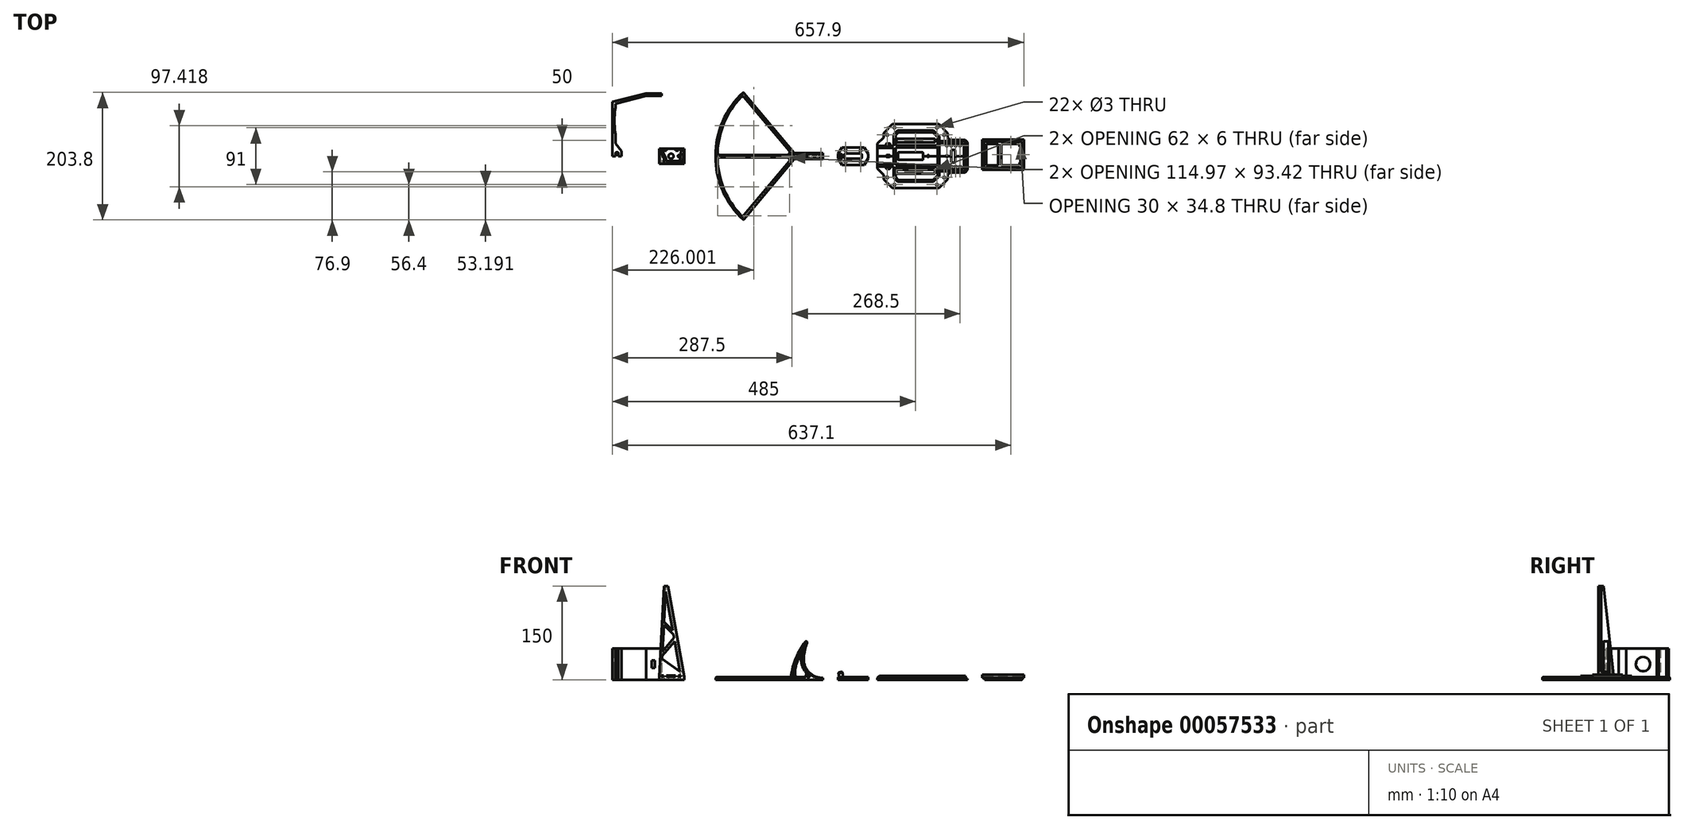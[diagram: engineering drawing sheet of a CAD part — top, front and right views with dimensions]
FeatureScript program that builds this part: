
annotation { "Feature Type Name" : "Feature", "Feature Type Description" : "" }
export const myFeature = defineFeature(function(context is Context, id is Id, definition is map)
    precondition{}
    {
        {
            var Q0;
            Q0=qCreatedBy(makeId("Front.planeOp"),FACE);
            var sketch = newSketch(context, id + "F0", { "sketchPlane" : qUnion([Q0])});
            skArc(sketch, "E0", {"start": v(23.8, 60.9) * mm, "mid": v(7.67, 32.1) * mm, "end": v(0, 0) * mm});
            skLineSegment(sketch, "E1", {"start": v(0, 0) * mm, "end": v(52, 0) * mm});
            skLineSegment(sketch, "E2", {"start": v(52, 0) * mm, "end": v(52, 3) * mm});
            skLineSegment(sketch, "E3", {"start": v(52, 3) * mm, "end": v(51, 3) * mm});
            skCircle(sketch, "E4", {"center": v(28.5, 4.8) * mm, "radius": 1.5 * mm});
            skArc(sketch, "E5", {"start": v(11.94, 32) * mm, "mid": v(11.4, 30.63) * mm, "end": v(10.87, 29.26) * mm});
            skLineSegment(sketch, "E6", {"start": v(7, 4) * mm, "end": v(22.45, 4) * mm});
            skArc(sketch, "E7", {"start": v(17.05, 31.14) * mm, "mid": v(19.78, 19.53) * mm, "end": v(26.35, 9.58) * mm});
            skArc(sketch, "E8", {"start": v(17.05, 31.14) * mm, "mid": v(14.83, 33.62) * mm, "end": v(11.94, 32) * mm});
            skLineSegment(sketch, "E9", {"start": v(22.45, 4) * mm, "end": v(26.35, 9.58) * mm});
            skArc(sketch, "E10", {"start": v(21.24, 36.77) * mm, "mid": v(28.5, 13.16) * mm, "end": v(51, 3) * mm});
            skArc(sketch, "E11", {"start": v(21, 51.66) * mm, "mid": v(16.42, 43.88) * mm, "end": v(12.45, 35.77) * mm});
            skArc(sketch, "E12", {"start": v(17.98, 34.71) * mm, "mid": v(15.37, 36.06) * mm, "end": v(12.45, 35.77) * mm});
            skArc(sketch, "E13", {"start": v(26.43, 59.54) * mm, "mid": v(25.7, 61.33) * mm, "end": v(23.8, 60.9) * mm});
            skArc(sketch, "E14", {"start": v(21, 51.66) * mm, "mid": v(19.19, 43.24) * mm, "end": v(17.98, 34.71) * mm});
            skLineSegment(sketch, "E15", {"start": v(26.43, 59.54) * mm, "end": v(26.12, 58.59) * mm});
            skArc(sketch, "E16", {"start": v(26.12, 58.59) * mm, "mid": v(23.16, 47.8) * mm, "end": v(21.24, 36.77) * mm});
            skArc(sketch, "E17", {"start": v(10.87, 29.26) * mm, "mid": v(7.97, 18.8) * mm, "end": v(7, 8) * mm});
            skLineSegment(sketch, "E18", {"start": v(7, 4) * mm, "end": v(7, 8) * mm});
            skSolve(sketch);
        }
        {
            var Q0;
            Q0=makeQuery(id+"F0.imprint","IMPRINT",FACE,{"disambiguationData":[TD([[makeQuery(id+"F0.imprint","IMPRINT",EDGE,{"derivedFrom":sQuery(id+"F0.wireOp",EDGE,"E0")}),1.0]])]});
            extrude(context, id + "F1", {"entities" : qUnion([Q0]), "depth" : (9.5 / 2) * mm});
        }
        {
            var Q0;
            Q0=makeQuery(id+"F1.opExtrude","SWEPT_EDGE",EDGE,{"disambiguationData":[OSD([sQuery(id+"F0.wireOp",EDGE,"E11"),sQuery(id+"F0.wireOp",EDGE,"E14")])]});
            fillet(context, id + "F2", {"entities" : qUnion([Q0]), "radius" : 0.75 * mm, "tangentPropagation" : true, "allowEdgeOverflow" : false});
        }
        {
            var Q0;
            Q0=makeQuery(id+"F1.opExtrude","SWEPT_EDGE",EDGE,{"disambiguationData":[OSD([sQuery(id+"F0.wireOp",EDGE,"E7"),sQuery(id+"F0.wireOp",EDGE,"E9")])]});
            var Q1;
            Q1=makeQuery(id+"F1.opExtrude","SWEPT_EDGE",EDGE,{"disambiguationData":[OSD([sQuery(id+"F0.wireOp",EDGE,"E6"),sQuery(id+"F0.wireOp",EDGE,"E9")])]});
            fillet(context, id + "F3", {"entities" : qUnion([Q0, Q1]), "radius" : 4 * mm, "tangentPropagation" : true, "allowEdgeOverflow" : false});
        }
        {
            var Q0;
            Q0=makeQuery(id+"F1.opExtrude","SWEPT_EDGE",EDGE,{"disambiguationData":[OSD([sQuery(id+"F0.wireOp",EDGE,"E5"),sQuery(id+"F0.wireOp",EDGE,"E6")])]});
            fillet(context, id + "F4", {"entities" : qUnion([Q0]), "radius" : 5 * mm, "tangentPropagation" : true, "allowEdgeOverflow" : false});
        }
        {
            var Q0;
            Q0=makeQuery(id+"F1.opExtrude","CAP_EDGE",EDGE,{"disambiguationData":[OSD([sQuery(id+"F0.wireOp",EDGE,"E0")])],"isStart":false});
            var Q1;
            Q1=makeQuery(id+"F1.opExtrude","CAP_EDGE",EDGE,{"disambiguationData":[OSD([sQuery(id+"F0.wireOp",EDGE,"E5")])],"isStart":false});
            chamfer(context, id + "F5", {"entities" : qUnion([Q0, Q1]), "width" : 1 * mm, "tangentPropagation" : true});
        }
        {
            var Q0;
            Q0=qCreatedBy(makeId("Top.planeOp"),FACE);
            cPlane(context, id + "F6", {"entities" : qUnion([Q0]), "cplaneType" : CPlaneType.OFFSET, "offset" : 2 * mm, "width" : 150 * mm, "height" : 150 * mm});
        }
        {
            var Q0;
            Q0=qCreatedBy(makeId("Top.planeOp"),FACE);
            var sketch = newSketch(context, id + "F7", { "sketchPlane" : qUnion([Q0])});
            skCircle(sketch, "E19", {"center": v(2.5, 0) * mm, "radius": 1.5 * mm});
            skCircle(sketch, "E20", {"center": v(20.5, 0) * mm, "radius": 2.5 * mm});
            skCircle(sketch, "E21", {"center": v(38.5, 0) * mm, "radius": 2 * mm});
            skCircle(sketch, "E22", {"center": v(48.5, 0) * mm, "radius": 1.5 * mm});
            skSolve(sketch);
        }
        {
            var Q0;
            Q0=makeQuery(id+"F7.imprint","IMPRINT",FACE,{"disambiguationData":[TD([[makeQuery(id+"F7.imprint","IMPRINT",EDGE,{"derivedFrom":sQuery(id+"F7.wireOp",EDGE,"E20")}),1.0]])]});
            var Q1;
            Q1=makeQuery(id+"F7.imprint","IMPRINT",FACE,{"disambiguationData":[TD([[makeQuery(id+"F7.imprint","IMPRINT",EDGE,{"derivedFrom":sQuery(id+"F7.wireOp",EDGE,"E21")}),1.0]])]});
            var Q2;
            Q2=makeQuery(id+"F7.imprint","IMPRINT",FACE,{"disambiguationData":[TD([[makeQuery(id+"F7.imprint","IMPRINT",EDGE,{"derivedFrom":sQuery(id+"F7.wireOp",EDGE,"E22")}),1.0]])]});
            extrude(context, id + "F8", {"entities" : qUnion([Q0, Q1, Q2]), "operationType" : NewBodyOperationType.REMOVE, "depth" : 8 * mm});
        }
        {
            var Q0;
            Q0=qCreatedBy(makeId("Top.planeOp"),FACE);
            var sketch = newSketch(context, id + "F9", { "sketchPlane" : qUnion([Q0])});
            skLineSegment(sketch, "E23", {"start": v(0, 0) * mm, "end": v(-119.5, 0) * mm});
            skLineSegment(sketch, "E24", {"start": v(10, 0) * mm, "end": v(-75.5, -101.9) * mm});
            skLineSegment(sketch, "E25", {"start": v(-116.52, -2) * mm, "end": v(-5.48, -2) * mm});
            skLineSegment(sketch, "E26", {"start": v(-2.41, -8.57) * mm, "end": v(-76.49, -96.85) * mm});
            skLineSegment(sketch, "E27", {"start": v(0, 0) * mm, "end": v(10, 0) * mm});
            skArc(sketch, "E28", {"start": v(-116.52, -2) * mm, "mid": v(-106.13, -53.49) * mm, "end": v(-76.49, -96.85) * mm});
            skArc(sketch, "E29", {"start": v(-119.5, 0) * mm, "mid": v(-108.46, -55.68) * mm, "end": v(-75.5, -101.9) * mm});
            skArc(sketch, "E30", {"start": v(-2.41, -8.57) * mm, "mid": v(-1.85, -4.3) * mm, "end": v(-5.48, -2) * mm});
            skSolve(sketch);
        }
        {
            var Q0;
            Q0 = qSketchRegion(id + "F9", true);
            extrude(context, id + "F10", {"entities" : qUnion([Q0]), "operationType" : NewBodyOperationType.ADD, "depth" : 4 * mm});
        }
        {
            var Q0;
            Q0=makeQuery(id+"F10.opExtrude","SWEPT_EDGE",EDGE,{"disambiguationData":[OSD([sQuery(id+"F9.wireOp",EDGE,"E25"),sQuery(id+"F9.wireOp",EDGE,"E26")])]});
            fillet(context, id + "F11", {"entities" : qUnion([Q0]), "radius" : 3 * mm, "tangentPropagation" : true, "allowEdgeOverflow" : false});
        }
        {
            var Q0;
            Q0=makeQuery(id+"F10.boolean.opBoolean","INTERSECT",EDGE,{"derivedFrom":[makeQuery(id+"F1.opExtrude","SWEPT_FACE",FACE,{"disambiguationData":[OSD([sQuery(id+"F0.wireOp",EDGE,"E0")])]}),makeQuery(id+"F10.opExtrude","CAP_FACE",FACE,{"disambiguationData":[OSD([sQuery(id+"F9.wireOp",EDGE,"E23"),sQuery(id+"F9.wireOp",EDGE,"E24"),sQuery(id+"F9.wireOp",EDGE,"E25"),sQuery(id+"F9.wireOp",EDGE,"E26"),sQuery(id+"F9.wireOp",EDGE,"E27"),sQuery(id+"F9.wireOp",EDGE,"E28"),sQuery(id+"F9.wireOp",EDGE,"E29"),sQuery(id+"F9.wireOp",EDGE,"E30")])],"isStart":false})]});
            var Q1;
            Q1=makeQuery(id+"F10.boolean.opBoolean","INTERSECT",EDGE,{"derivedFrom":[makeQuery(id+"F5.opChamfer","BLEND_FACE",FACE,{"disambiguationData":[OSD([sQuery(id+"F0.wireOp",EDGE,"E0")])]}),makeQuery(id+"F10.opExtrude","CAP_FACE",FACE,{"disambiguationData":[OSD([sQuery(id+"F9.wireOp",EDGE,"E23"),sQuery(id+"F9.wireOp",EDGE,"E24"),sQuery(id+"F9.wireOp",EDGE,"E25"),sQuery(id+"F9.wireOp",EDGE,"E26"),sQuery(id+"F9.wireOp",EDGE,"E27"),sQuery(id+"F9.wireOp",EDGE,"E28"),sQuery(id+"F9.wireOp",EDGE,"E29"),sQuery(id+"F9.wireOp",EDGE,"E30")])],"isStart":false})]});
            fillet(context, id + "F12", {"entities" : qUnion([Q0, Q1]), "radius" : 2 * mm, "tangentPropagation" : true, "allowEdgeOverflow" : false});
        }
        {
            var Q0;
            Q0=makeQuery(id+"F7.imprint","IMPRINT",FACE,{"disambiguationData":[TD([[makeQuery(id+"F7.imprint","IMPRINT",EDGE,{"derivedFrom":sQuery(id+"F7.wireOp",EDGE,"E19")}),1.0]])]});
            extrude(context, id + "F13", {"entities" : qUnion([Q0]), "operationType" : NewBodyOperationType.REMOVE, "endBound" : BoundingType.THROUGH_ALL, "depth" : 25 * mm});
        }
        {
            var Q0;
            Q0=qCreatedBy(id+"F6.planeOp",FACE);
            var sketch = newSketch(context, id + "F14", { "sketchPlane" : qUnion([Q0])});
            skCircle(sketch, "E31", {"center": v(48.5, 0) * mm, "radius": 2.5 * mm});
            skCircle(sketch, "E32", {"center": v(2.5, 0) * mm, "radius": 2.5 * mm});
            skSolve(sketch);
        }
        {
            var Q0;
            Q0 = qSketchRegion(id + "F14", true);
            extrude(context, id + "F15", {"entities" : qUnion([Q0]), "operationType" : NewBodyOperationType.REMOVE, "depth" : 25 * mm});
        }
        {
            var Q0;
            Q0=makeQuery(id+"F10.opExtrude","CAP_EDGE",EDGE,{"disambiguationData":[OSD([sQuery(id+"F9.wireOp",EDGE,"E29")])],"isStart":false});
            chamfer(context, id + "F16", {"entities" : qUnion([Q0]), "width" : 1 * mm});
        }
        {
            var Q0;
            Q0=makeQuery(id+"F10.opExtrude","SWEPT_FACE",FACE,{"disambiguationData":[OSD([sQuery(id+"F9.wireOp",EDGE,"E24")])]});
            cPlane(context, id + "F17", {"entities" : qUnion([Q0]), "cplaneType" : CPlaneType.OFFSET, "offset" : 2 * mm, "oppositeDirection" : true, "width" : 150 * mm, "height" : 150 * mm});
        }
        {
            var Q0;
            Q0=qCreatedBy(id+"F17.planeOp",FACE);
            var sketch = newSketch(context, id + "F18", { "sketchPlane" : qUnion([Q0])});
            skLineSegment(sketch, "E33", {"start": v(-6.45, 4) * mm, "end": v(-0.45, 4) * mm});
            skLineSegment(sketch, "E34", {"start": v(-0.45, 4) * mm, "end": v(-0.45, 8) * mm});
            skLineSegment(sketch, "E35", {"start": v(-0.45, 8) * mm, "end": v(-6.45, 4) * mm});
            skSolve(sketch);
        }
        {
            var Q0;
            Q0=makeQuery(id+"F1.opExtrude","SWEPT_BODY",BODY,{"disambiguationData":[OSD([sQuery(id+"F0.wireOp",EDGE,"E0"),sQuery(id+"F0.wireOp",EDGE,"E1"),sQuery(id+"F0.wireOp",EDGE,"E2"),sQuery(id+"F0.wireOp",EDGE,"E3"),sQuery(id+"F0.wireOp",EDGE,"E4"),sQuery(id+"F0.wireOp",EDGE,"E5"),sQuery(id+"F0.wireOp",EDGE,"E6"),sQuery(id+"F0.wireOp",EDGE,"E7"),sQuery(id+"F0.wireOp",EDGE,"E8"),sQuery(id+"F0.wireOp",EDGE,"E9"),sQuery(id+"F0.wireOp",EDGE,"E10"),sQuery(id+"F0.wireOp",EDGE,"E11"),sQuery(id+"F0.wireOp",EDGE,"E12"),sQuery(id+"F0.wireOp",EDGE,"E13"),sQuery(id+"F0.wireOp",EDGE,"E14"),sQuery(id+"F0.wireOp",EDGE,"E15"),sQuery(id+"F0.wireOp",EDGE,"E16")])]});
            var Q1;
            Q1=qCreatedBy(makeId("Front.planeOp"),FACE);
            mirror(context, id + "F19", {"operationType" : NewBodyOperationType.ADD, "entities" : qUnion([Q0]), "mirrorPlane" : qUnion([Q1])});
        }
        {
            var Q0;
            Q0=qCreatedBy(makeId("Right.planeOp"),FACE);
            cPlane(context, id + "F20", {"entities" : qUnion([Q0]), "cplaneType" : CPlaneType.OFFSET, "offset" : 100 * mm, "width" : 150 * mm, "height" : 150 * mm});
        }
        {
            var Q0;
            Q0=qCreatedBy(makeId("Top.planeOp"),FACE);
            var sketch = newSketch(context, id + "F21", { "sketchPlane" : qUnion([Q0])});
            skCircle(sketch, "E36", {"center": v(88, 9) * mm, "radius": 1.5 * mm});
            skCircle(sketch, "E37", {"center": v(112, 9) * mm, "radius": 1.5 * mm});
            skCircle(sketch, "E38", {"center": v(88, -9) * mm, "radius": 1.5 * mm});
            skCircle(sketch, "E39", {"center": v(112, -9) * mm, "radius": 1.5 * mm});
            skLineSegment(sketch, "E40.bottom", {"start": v(86, 4) * mm, "end": v(114, 4) * mm});
            skLineSegment(sketch, "E40.top", {"start": v(86, -4) * mm, "end": v(114, -4) * mm});
            skLineSegment(sketch, "E40.left", {"start": v(86, 4) * mm, "end": v(86, -4) * mm});
            skLineSegment(sketch, "E40.right", {"start": v(114, 4) * mm, "end": v(114, -4) * mm});
            skLineSegment(sketch, "E41.bottom", {"start": v(82, 14) * mm, "end": v(118, 14) * mm});
            skLineSegment(sketch, "E41.top", {"start": v(82, -14) * mm, "end": v(118, -14) * mm});
            skLineSegment(sketch, "E41.left", {"start": v(82, 14) * mm, "end": v(82, -14) * mm});
            skLineSegment(sketch, "E41.right", {"start": v(118, 14) * mm, "end": v(118, -14) * mm});
            skPoint(sketch, "E42", {"position": v(82, 0) * mm});
            skLineSegment(sketch, "E43.bottom", {"start": v(88, 9) * mm, "end": v(112, 9) * mm, "construction": true});
            skLineSegment(sketch, "E43.top", {"start": v(88, -9) * mm, "end": v(112, -9) * mm, "construction": true});
            skLineSegment(sketch, "E43.left", {"start": v(88, 9) * mm, "end": v(88, -9) * mm, "construction": true});
            skLineSegment(sketch, "E43.right", {"start": v(112, 9) * mm, "end": v(112, -9) * mm, "construction": true});
            skPoint(sketch, "E44", {"position": v(86, 0) * mm});
            skPoint(sketch, "E45", {"position": v(88, 0) * mm});
            skPoint(sketch, "E46", {"position": v(100, -9) * mm});
            skPoint(sketch, "E47", {"position": v(100, -4) * mm});
            skPoint(sketch, "E48", {"position": v(100, -14) * mm});
            skSolve(sketch);
        }
        {
            var Q0;
            Q0=makeQuery(id+"F21.imprint","IMPRINT",FACE,{"disambiguationData":[TD([[makeQuery(id+"F21.imprint","IMPRINT",EDGE,{"derivedFrom":sQuery(id+"F21.wireOp",EDGE,"E36")}),-1.0]])]});
            extrude(context, id + "F22", {"entities" : qUnion([Q0]), "depth" : 4 * mm});
        }
        {
            var Q0;
            Q0=makeQuery(id+"F22.opExtrude","SWEPT_EDGE",EDGE,{"disambiguationData":[OSD([sQuery(id+"F21.wireOp",EDGE,"E40.bottom"),sQuery(id+"F21.wireOp",EDGE,"E40.left")])]});
            var Q1;
            Q1=makeQuery(id+"F22.opExtrude","SWEPT_EDGE",EDGE,{"disambiguationData":[OSD([sQuery(id+"F21.wireOp",EDGE,"E40.top"),sQuery(id+"F21.wireOp",EDGE,"E40.left")])]});
            var Q2;
            Q2=makeQuery(id+"F22.opExtrude","SWEPT_EDGE",EDGE,{"disambiguationData":[OSD([sQuery(id+"F21.wireOp",EDGE,"E40.top"),sQuery(id+"F21.wireOp",EDGE,"E40.right")])]});
            var Q3;
            Q3=makeQuery(id+"F22.opExtrude","SWEPT_EDGE",EDGE,{"disambiguationData":[OSD([sQuery(id+"F21.wireOp",EDGE,"E40.bottom"),sQuery(id+"F21.wireOp",EDGE,"E40.right")])]});
            fillet(context, id + "F23", {"entities" : qUnion([Q0, Q1, Q2, Q3]), "radius" : 2 * mm, "tangentPropagation" : true, "allowEdgeOverflow" : false});
        }
        {
            var Q0;
            Q0=qCreatedBy(makeId("Top.planeOp"),FACE);
            var sketch = newSketch(context, id + "F24", { "sketchPlane" : qUnion([Q0])});
            skLineSegment(sketch, "E49", {"start": v(118, 14) * mm, "end": v(118, -14) * mm});
            skLineSegment(sketch, "E50", {"start": v(118, -14) * mm, "end": v(124, -3.6) * mm});
            skLineSegment(sketch, "E51", {"start": v(124, -3.6) * mm, "end": v(124, 3.6) * mm});
            skLineSegment(sketch, "E52", {"start": v(124, 3.6) * mm, "end": v(118, 14) * mm});
            skLineSegment(sketch, "E53", {"start": v(82, 14) * mm, "end": v(82, -14) * mm});
            skLineSegment(sketch, "E54", {"start": v(82, -14) * mm, "end": v(76, -3.6) * mm});
            skLineSegment(sketch, "E55", {"start": v(76, -3.6) * mm, "end": v(76, 3.6) * mm});
            skLineSegment(sketch, "E56", {"start": v(76, 3.6) * mm, "end": v(82, 14) * mm});
            skSolve(sketch);
        }
        {
            var Q0;
            Q0 = qSketchRegion(id + "F24", true);
            var Q1;
            Q1=makeQuery(id+"F22.opExtrude","CAP_FACE",FACE,{"disambiguationData":[OSD([sQuery(id+"F21.wireOp",EDGE,"E36"),sQuery(id+"F21.wireOp",EDGE,"E37"),sQuery(id+"F21.wireOp",EDGE,"E38"),sQuery(id+"F21.wireOp",EDGE,"E39"),sQuery(id+"F21.wireOp",EDGE,"E40.bottom"),sQuery(id+"F21.wireOp",EDGE,"E40.top"),sQuery(id+"F21.wireOp",EDGE,"E40.left"),sQuery(id+"F21.wireOp",EDGE,"E40.right"),sQuery(id+"F21.wireOp",EDGE,"E41.bottom"),sQuery(id+"F21.wireOp",EDGE,"E41.top"),sQuery(id+"F21.wireOp",EDGE,"E41.left"),sQuery(id+"F21.wireOp",EDGE,"E41.right")])],"isStart":false});
            extrude(context, id + "F25", {"entities" : qUnion([Q0]), "operationType" : NewBodyOperationType.ADD, "endBound" : BoundingType.UP_TO_SURFACE, "endBoundEntityFace" : qUnion([Q1]), "depth" : 25 * mm});
        }
        {
            var Q0;
            Q0=qCreatedBy(makeId("Front.planeOp"),FACE);
            var sketch = newSketch(context, id + "F26", { "sketchPlane" : qUnion([Q0])});
            skLineSegment(sketch, "E57", {"start": v(81, 4) * mm, "end": v(85.92, 4.87) * mm});
            skSolve(sketch);
        }
        {
            var Q0;
            Q0=sQuery(id+"F26.wireOp",EDGE,"E57");
            var Q1;
            Q1=qCreatedBy(makeId("Front.planeOp"),FACE);
            cPlane(context, id + "F27", {"entities" : qUnion([Q0, Q1]), "cplaneType" : CPlaneType.LINE_ANGLE, "offset" : 150 * mm, "angle" : 100 * degree, "width" : 150 * mm, "height" : 150 * mm});
        }
        {
            var Q0;
            Q0=qCreatedBy(id+"F27.planeOp",FACE);
            var sketch = newSketch(context, id + "F28", { "sketchPlane" : qUnion([Q0])});
            skCircle(sketch, "E58", {"center": v(80.48, 0.7) * mm, "radius": 2 * mm});
            skCircle(sketch, "E59", {"center": v(80.48, 0.7) * mm, "radius": 3 * mm});
            skSolve(sketch);
        }
        {
            var Q0;
            Q0 = qSketchRegion(id + "F28", true);
            var Q1;
            Q1=makeQuery(id+"F25.boolean.opBoolean","MERGE",FACE,{"derivedFrom":[makeQuery(id+"F22.opExtrude","CAP_FACE",FACE,{"disambiguationData":[OSD([sQuery(id+"F21.wireOp",EDGE,"E36"),sQuery(id+"F21.wireOp",EDGE,"E37"),sQuery(id+"F21.wireOp",EDGE,"E38"),sQuery(id+"F21.wireOp",EDGE,"E39"),sQuery(id+"F21.wireOp",EDGE,"E40.bottom"),sQuery(id+"F21.wireOp",EDGE,"E40.top"),sQuery(id+"F21.wireOp",EDGE,"E40.left"),sQuery(id+"F21.wireOp",EDGE,"E40.right"),sQuery(id+"F21.wireOp",EDGE,"E41.bottom"),sQuery(id+"F21.wireOp",EDGE,"E41.top"),sQuery(id+"F21.wireOp",EDGE,"E41.left"),sQuery(id+"F21.wireOp",EDGE,"E41.right")])],"isStart":false}),makeQuery(id+"F25.opExtrude","CAP_FACE",FACE,{"disambiguationData":[OSD([sQuery(id+"F24.wireOp",EDGE,"E49"),sQuery(id+"F24.wireOp",EDGE,"E50"),sQuery(id+"F24.wireOp",EDGE,"E51"),sQuery(id+"F24.wireOp",EDGE,"E52")])],"isStart":false}),makeQuery(id+"F25.opExtrude","CAP_FACE",FACE,{"disambiguationData":[OSD([sQuery(id+"F24.wireOp",EDGE,"E53"),sQuery(id+"F24.wireOp",EDGE,"E54"),sQuery(id+"F24.wireOp",EDGE,"E55"),sQuery(id+"F24.wireOp",EDGE,"E56")])],"isStart":false})]});
            extrude(context, id + "F29", {"entities" : qUnion([Q0]), "operationType" : NewBodyOperationType.ADD, "depth" : 8 * mm, "hasSecondDirection" : true, "secondDirectionBound" : SecondDirectionBoundingType.UP_TO_SURFACE, "secondDirectionOppositeDirection" : true, "secondDirectionBoundEntityFace" : qUnion([Q1]), "secondDirectionDepth" : 25 * mm});
        }
        {
            var Q0;
            Q0=qCreatedBy(makeId("Right.planeOp"),FACE);
            cPlane(context, id + "F30", {"entities" : qUnion([Q0]), "cplaneType" : CPlaneType.OFFSET, "offset" : 200 * mm, "width" : 150 * mm, "height" : 150 * mm});
        }
        {
            var Q0;
            Q0=qCreatedBy(makeId("Top.planeOp"),FACE);
            var sketch = newSketch(context, id + "F31", { "sketchPlane" : qUnion([Q0])});
            skLineSegment(sketch, "E60", {"start": v(283, 0) * mm, "end": v(283, -26) * mm});
            skLineSegment(sketch, "E61", {"start": v(283, -26) * mm, "end": v(251, -26) * mm});
            skLineSegment(sketch, "E62", {"start": v(251, -26) * mm, "end": v(251, -36.99) * mm});
            skLineSegment(sketch, "E63", {"start": v(251, -36.99) * mm, "end": v(236.99, -51) * mm});
            skLineSegment(sketch, "E64", {"start": v(236.99, -51) * mm, "end": v(163.01, -51) * mm});
            skLineSegment(sketch, "E65", {"start": v(163.01, -51) * mm, "end": v(149, -36.99) * mm});
            skLineSegment(sketch, "E66", {"start": v(149, -36.99) * mm, "end": v(149, -30) * mm});
            skPoint(sketch, "E67", {"position": v(200, -51) * mm});
            skLineSegment(sketch, "E68", {"start": v(154.5, 0) * mm, "end": v(154.5, -34) * mm, "construction": true});
            skLineSegment(sketch, "E69", {"start": v(154.5, -34) * mm, "end": v(166, -45.5) * mm, "construction": true});
            skLineSegment(sketch, "E70", {"start": v(166, -45.5) * mm, "end": v(234, -45.5) * mm, "construction": true});
            skLineSegment(sketch, "E71", {"start": v(234, -45.5) * mm, "end": v(245.5, -34) * mm, "construction": true});
            skLineSegment(sketch, "E72", {"start": v(245.5, -34) * mm, "end": v(245.5, 0) * mm, "construction": true});
            skPoint(sketch, "E73", {"position": v(200, -45.5) * mm});
            skCircle(sketch, "E74", {"center": v(154.5, -34) * mm, "radius": 1.5 * mm});
            skCircle(sketch, "E75", {"center": v(166, -45.5) * mm, "radius": 1.5 * mm});
            skCircle(sketch, "E76", {"center": v(234, -45.5) * mm, "radius": 1.5 * mm});
            skCircle(sketch, "E77", {"center": v(245.5, -34) * mm, "radius": 1.5 * mm});
            skCircle(sketch, "E78", {"center": v(250, -17) * mm, "radius": 1.5 * mm});
            skCircle(sketch, "E79", {"center": v(257, -17) * mm, "radius": 1.5 * mm});
            skCircle(sketch, "E80", {"center": v(271, -17) * mm, "radius": 1.5 * mm});
            skCircle(sketch, "E81", {"center": v(264, -17) * mm, "radius": 1.5 * mm});
            skLineSegment(sketch, "E82", {"start": v(250, -17) * mm, "end": v(257, -17) * mm, "construction": true});
            skLineSegment(sketch, "E83", {"start": v(264, -17) * mm, "end": v(257, -17) * mm, "construction": true});
            skLineSegment(sketch, "E84", {"start": v(271, -17) * mm, "end": v(264, -17) * mm, "construction": true});
            skLineSegment(sketch, "E85", {"start": v(139, 0) * mm, "end": v(139, -20) * mm});
            skLineSegment(sketch, "E86", {"start": v(139, -20) * mm, "end": v(149, -30) * mm});
            skLineSegment(sketch, "E87.trimOffspring", {"start": v(139, 0) * mm, "end": v(153, 0) * mm});
            skLineSegment(sketch, "E88", {"start": v(172, 0) * mm, "end": v(172, -6) * mm});
            skLineSegment(sketch, "E89", {"start": v(172, -6) * mm, "end": v(212, -6) * mm});
            skLineSegment(sketch, "E90", {"start": v(212, -6) * mm, "end": v(212, 0) * mm});
            skLineSegment(sketch, "E91.trimOffspring", {"start": v(212, 0) * mm, "end": v(218.5, 0) * mm});
            skLineSegment(sketch, "E92", {"start": v(257, 0) * mm, "end": v(257, -10) * mm});
            skLineSegment(sketch, "E93", {"start": v(257, -10) * mm, "end": v(263, -10) * mm});
            skLineSegment(sketch, "E94", {"start": v(263, -10) * mm, "end": v(263, 0) * mm});
            skLineSegment(sketch, "E95.trimOffspring", {"start": v(263, 0) * mm, "end": v(283, 0) * mm});
            skLineSegment(sketch, "E96.bottom", {"start": v(169, -22) * mm, "end": v(231, -22) * mm});
            skLineSegment(sketch, "E96.top", {"start": v(169, -28) * mm, "end": v(231, -28) * mm});
            skLineSegment(sketch, "E96.left", {"start": v(169, -22) * mm, "end": v(169, -28) * mm});
            skLineSegment(sketch, "E96.right", {"start": v(231, -22) * mm, "end": v(231, -28) * mm});
            skPoint(sketch, "E97", {"position": v(200, -28) * mm});
            skArc(sketch, "E98", {"start": v(248.5, 0) * mm, "mid": v(250, -1.5) * mm, "end": v(251.5, 0) * mm});
            skArc(sketch, "E99", {"start": v(218.5, 0) * mm, "mid": v(220, -1.5) * mm, "end": v(221.5, 0) * mm});
            skLineSegment(sketch, "E100", {"start": v(250, -17) * mm, "end": v(250, 0) * mm, "construction": true});
            skLineSegment(sketch, "E101.trimOffspring", {"start": v(221.5, 0) * mm, "end": v(248.5, 0) * mm});
            skLineSegment(sketch, "E102.trimOffspring", {"start": v(251.5, 0) * mm, "end": v(257, 0) * mm});
            skLineSegment(sketch, "E103.bottom", {"start": v(153, -17.5) * mm, "end": v(159, -17.5) * mm});
            skLineSegment(sketch, "E103.top", {"start": v(153, -20.5) * mm, "end": v(159, -20.5) * mm});
            skLineSegment(sketch, "E103.left", {"start": v(153, -17.5) * mm, "end": v(153, -20.5) * mm});
            skLineSegment(sketch, "E103.right", {"start": v(159, -17.5) * mm, "end": v(159, -20.5) * mm});
            skLineSegment(sketch, "E104", {"start": v(153, 0) * mm, "end": v(153, -1.5) * mm});
            skLineSegment(sketch, "E105", {"start": v(153, -1.5) * mm, "end": v(159, -1.5) * mm});
            skLineSegment(sketch, "E106", {"start": v(159, -1.5) * mm, "end": v(159, 0) * mm});
            skLineSegment(sketch, "E107.trimOffspring", {"start": v(159, 0) * mm, "end": v(172, 0) * mm});
            skSolve(sketch);
        }
        {
            var Q0;
            Q0=makeQuery(id+"F31.imprint","IMPRINT",FACE,{"disambiguationData":[TD([[makeQuery(id+"F31.imprint","IMPRINT",EDGE,{"derivedFrom":sQuery(id+"F31.wireOp",EDGE,"E60")}),-1.0]])]});
            extrude(context, id + "F32", {"entities" : qUnion([Q0]), "depth" : 2 * mm});
        }
        {
            var Q0;
            Q0=qCreatedBy(makeId("Front.planeOp"),FACE);
            cPlane(context, id + "F33", {"entities" : qUnion([Q0]), "cplaneType" : CPlaneType.OFFSET, "offset" : 48 * mm, "width" : 150 * mm, "height" : 150 * mm});
        }
        {
            var Q0;
            Q0=qCreatedBy(id+"F33.planeOp",FACE);
            var sketch = newSketch(context, id + "F34", { "sketchPlane" : qUnion([Q0])});
            skCircle(sketch, "E108", {"center": v(195, 3.5) * mm, "radius": 1 * mm});
            skCircle(sketch, "E109", {"center": v(205, 3.5) * mm, "radius": 1 * mm});
            skLineSegment(sketch, "E110", {"start": v(190.98, 2) * mm, "end": v(193, 5.5) * mm});
            skLineSegment(sketch, "E111", {"start": v(193, 5.5) * mm, "end": v(207, 5.5) * mm});
            skLineSegment(sketch, "E112", {"start": v(207, 5.5) * mm, "end": v(209.02, 2) * mm});
            skLineSegment(sketch, "E113", {"start": v(209.02, 2) * mm, "end": v(190.98, 2) * mm});
            skLineSegment(sketch, "E114", {"start": v(195, 3.5) * mm, "end": v(205, 3.5) * mm, "construction": true});
            skPoint(sketch, "E115", {"position": v(200, 3.5) * mm});
            skPoint(sketch, "E116", {"position": v(200, 2) * mm});
            skSolve(sketch);
        }
        {
            var Q0;
            Q0=makeQuery(id+"F32.opExtrude","CAP_FACE",FACE,{"disambiguationData":[OSD([sQuery(id+"F31.wireOp",EDGE,"E60"),sQuery(id+"F31.wireOp",EDGE,"E61"),sQuery(id+"F31.wireOp",EDGE,"E62"),sQuery(id+"F31.wireOp",EDGE,"E63"),sQuery(id+"F31.wireOp",EDGE,"E64"),sQuery(id+"F31.wireOp",EDGE,"E65"),sQuery(id+"F31.wireOp",EDGE,"E66"),sQuery(id+"F31.wireOp",EDGE,"E74"),sQuery(id+"F31.wireOp",EDGE,"E75"),sQuery(id+"F31.wireOp",EDGE,"E76"),sQuery(id+"F31.wireOp",EDGE,"E77"),sQuery(id+"F31.wireOp",EDGE,"E78"),sQuery(id+"F31.wireOp",EDGE,"E79"),sQuery(id+"F31.wireOp",EDGE,"E80"),sQuery(id+"F31.wireOp",EDGE,"E81"),sQuery(id+"F31.wireOp",EDGE,"E85"),sQuery(id+"F31.wireOp",EDGE,"E86"),sQuery(id+"F31.wireOp",EDGE,"E87.trimOffspring"),sQuery(id+"F31.wireOp",EDGE,"E88"),sQuery(id+"F31.wireOp",EDGE,"E89"),sQuery(id+"F31.wireOp",EDGE,"E90"),sQuery(id+"F31.wireOp",EDGE,"E91.trimOffspring"),sQuery(id+"F31.wireOp",EDGE,"E92"),sQuery(id+"F31.wireOp",EDGE,"E93"),sQuery(id+"F31.wireOp",EDGE,"E94"),sQuery(id+"F31.wireOp",EDGE,"E95.trimOffspring"),sQuery(id+"F31.wireOp",EDGE,"E96.bottom"),sQuery(id+"F31.wireOp",EDGE,"E96.top"),sQuery(id+"F31.wireOp",EDGE,"E96.left"),sQuery(id+"F31.wireOp",EDGE,"E96.right"),sQuery(id+"F31.wireOp",EDGE,"E98"),sQuery(id+"F31.wireOp",EDGE,"E99"),sQuery(id+"F31.wireOp",EDGE,"E101.trimOffspring"),sQuery(id+"F31.wireOp",EDGE,"E102.trimOffspring"),sQuery(id+"F31.wireOp",EDGE,"E103.bottom"),sQuery(id+"F31.wireOp",EDGE,"E103.top"),sQuery(id+"F31.wireOp",EDGE,"E103.left"),sQuery(id+"F31.wireOp",EDGE,"E103.right"),sQuery(id+"F31.wireOp",EDGE,"E104"),sQuery(id+"F31.wireOp",EDGE,"E105"),sQuery(id+"F31.wireOp",EDGE,"E106"),sQuery(id+"F31.wireOp",EDGE,"E107.trimOffspring")])],"isStart":false});
            var sketch = newSketch(context, id + "F35", { "sketchPlane" : qUnion([Q0])});
            skLineSegment(sketch, "E117", {"start": v(235, 0) * mm, "end": v(238, 0) * mm});
            skLineSegment(sketch, "E118", {"start": v(238, 0) * mm, "end": v(238, -21) * mm});
            skLineSegment(sketch, "E119", {"start": v(280, 0) * mm, "end": v(280, -24) * mm});
            skLineSegment(sketch, "E120", {"start": v(238, -31.6) * mm, "end": v(228.6, -41) * mm});
            skLineSegment(sketch, "E121", {"start": v(228.6, -41) * mm, "end": v(171.4, -41) * mm});
            skLineSegment(sketch, "E122", {"start": v(171.4, -41) * mm, "end": v(165, -34.6) * mm});
            skLineSegment(sketch, "E123", {"start": v(165, 0) * mm, "end": v(168, 0) * mm});
            skLineSegment(sketch, "E124", {"start": v(168, 0) * mm, "end": v(168, -14) * mm});
            skLineSegment(sketch, "E125", {"start": v(168, -14) * mm, "end": v(235, -14) * mm});
            skLineSegment(sketch, "E126", {"start": v(235, -14) * mm, "end": v(235, 0) * mm});
            skLineSegment(sketch, "E127", {"start": v(235, -17) * mm, "end": v(168, -17) * mm});
            skLineSegment(sketch, "E128", {"start": v(168, -17) * mm, "end": v(168, -33.36) * mm});
            skLineSegment(sketch, "E129", {"start": v(168, -33.36) * mm, "end": v(172.64, -38) * mm});
            skLineSegment(sketch, "E130", {"start": v(172.64, -38) * mm, "end": v(227.36, -38) * mm});
            skLineSegment(sketch, "E131", {"start": v(227.36, -38) * mm, "end": v(235, -30.36) * mm});
            skLineSegment(sketch, "E132", {"start": v(235, -30.36) * mm, "end": v(235, -17) * mm});
            skLineSegment(sketch, "E133", {"start": v(280, -24) * mm, "end": v(238, -24) * mm});
            skLineSegment(sketch, "E134", {"start": v(238, -24) * mm, "end": v(238, -31.6) * mm});
            skLineSegment(sketch, "E135", {"start": v(238, -21) * mm, "end": v(277, -21) * mm});
            skLineSegment(sketch, "E136", {"start": v(277, -21) * mm, "end": v(277, 0) * mm});
            skLineSegment(sketch, "E137", {"start": v(277, 0) * mm, "end": v(280, 0) * mm});
            skLineSegment(sketch, "E138", {"start": v(165, -34.6) * mm, "end": v(165, -16.5) * mm});
            skLineSegment(sketch, "E139", {"start": v(165, -16.5) * mm, "end": v(139, -16.5) * mm});
            skLineSegment(sketch, "E140", {"start": v(139, -16.5) * mm, "end": v(139, -13.5) * mm});
            skLineSegment(sketch, "E141", {"start": v(139, -13.5) * mm, "end": v(165, -13.5) * mm});
            skLineSegment(sketch, "E142", {"start": v(165, -13.5) * mm, "end": v(165, 0) * mm});
            skSolve(sketch);
        }
        {
            var Q0;
            Q0 = qSketchRegion(id + "F35", true);
            extrude(context, id + "F36", {"entities" : qUnion([Q0]), "operationType" : NewBodyOperationType.ADD, "depth" : 4 * mm});
        }
        {
            var Q0;
            Q0=makeQuery(id+"F36.opExtrude","SWEPT_FACE",FACE,{"disambiguationData":[OSD([sQuery(id+"F35.wireOp",EDGE,"E119")])]});
            var sketch = newSketch(context, id + "F37", { "sketchPlane" : qUnion([Q0])});
            skLineSegment(sketch, "E143", {"start": v(-12, 6) * mm, "end": v(0, 6) * mm});
            skLineSegment(sketch, "E144", {"start": v(0, 6) * mm, "end": v(0, 3) * mm});
            skLineSegment(sketch, "E145", {"start": v(0, 3) * mm, "end": v(-9, 3) * mm});
            skLineSegment(sketch, "E146", {"start": v(-9, 3) * mm, "end": v(-12, 6) * mm});
            skSolve(sketch);
        }
        {
            var Q0;
            Q0 = qSketchRegion(id + "F37", true);
            extrude(context, id + "F38", {"entities" : qUnion([Q0]), "operationType" : NewBodyOperationType.REMOVE, "oppositeDirection" : true, "depth" : 80 * mm});
        }
        {
            var Q0;
            Q0=makeQuery(id+"F36.opExtrude","CAP_EDGE",EDGE,{"disambiguationData":[OSD([sQuery(id+"F35.wireOp",EDGE,"E140")])],"isStart":false});
            var Q1;
            Q1=makeQuery(id+"F36.opExtrude","SWEPT_EDGE",EDGE,{"disambiguationData":[OSD([sQuery(id+"F35.wireOp",EDGE,"E119"),sQuery(id+"F35.wireOp",EDGE,"E133")])]});
            var Q2;
            Q2=makeQuery(id+"F36.opExtrude","SWEPT_EDGE",EDGE,{"disambiguationData":[OSD([sQuery(id+"F35.wireOp",EDGE,"E135"),sQuery(id+"F35.wireOp",EDGE,"E136")])]});
            chamfer(context, id + "F39", {"entities" : qUnion([Q0, Q1, Q2]), "width" : 3 * mm, "tangentPropagation" : true});
        }
        {
            var Q0;
            Q0=makeQuery(id+"F32.opExtrude","SWEPT_EDGE",EDGE,{"disambiguationData":[OSD([sQuery(id+"F31.wireOp",EDGE,"E61"),sQuery(id+"F31.wireOp",EDGE,"E62")])]});
            var Q1;
            Q1=makeQuery(id+"F32.opExtrude","SWEPT_EDGE",EDGE,{"disambiguationData":[OSD([sQuery(id+"F31.wireOp",EDGE,"E60"),sQuery(id+"F31.wireOp",EDGE,"E61")])]});
            chamfer(context, id + "F40", {"entities" : qUnion([Q0, Q1]), "width" : 4 * mm, "tangentPropagation" : true});
        }
        {
            var Q0;
            Q0=makeQuery(id+"F32.opExtrude","SWEPT_EDGE",EDGE,{"disambiguationData":[OSD([sQuery(id+"F31.wireOp",EDGE,"E103.bottom"),sQuery(id+"F31.wireOp",EDGE,"E103.left")])]});
            var Q1;
            Q1=makeQuery(id+"F32.opExtrude","SWEPT_EDGE",EDGE,{"disambiguationData":[OSD([sQuery(id+"F31.wireOp",EDGE,"E103.bottom"),sQuery(id+"F31.wireOp",EDGE,"E103.right")])]});
            var Q2;
            Q2=makeQuery(id+"F32.opExtrude","SWEPT_EDGE",EDGE,{"disambiguationData":[OSD([sQuery(id+"F31.wireOp",EDGE,"E103.top"),sQuery(id+"F31.wireOp",EDGE,"E103.left")])]});
            var Q3;
            Q3=makeQuery(id+"F32.opExtrude","SWEPT_EDGE",EDGE,{"disambiguationData":[OSD([sQuery(id+"F31.wireOp",EDGE,"E103.top"),sQuery(id+"F31.wireOp",EDGE,"E103.right")])]});
            var Q4;
            Q4=makeQuery(id+"F32.opExtrude","SWEPT_EDGE",EDGE,{"disambiguationData":[OSD([sQuery(id+"F31.wireOp",EDGE,"E105"),sQuery(id+"F31.wireOp",EDGE,"E106")])]});
            var Q5;
            Q5=makeQuery(id+"F32.opExtrude","SWEPT_EDGE",EDGE,{"disambiguationData":[OSD([sQuery(id+"F31.wireOp",EDGE,"E104"),sQuery(id+"F31.wireOp",EDGE,"E105")])]});
            var Q6;
            Q6=makeQuery(id+"F32.opExtrude","SWEPT_EDGE",EDGE,{"disambiguationData":[OSD([sQuery(id+"F31.wireOp",EDGE,"E88"),sQuery(id+"F31.wireOp",EDGE,"E89")])]});
            var Q7;
            Q7=makeQuery(id+"F32.opExtrude","SWEPT_EDGE",EDGE,{"disambiguationData":[OSD([sQuery(id+"F31.wireOp",EDGE,"E96.top"),sQuery(id+"F31.wireOp",EDGE,"E96.left")])]});
            var Q8;
            Q8=makeQuery(id+"F32.opExtrude","SWEPT_EDGE",EDGE,{"disambiguationData":[OSD([sQuery(id+"F31.wireOp",EDGE,"E96.bottom"),sQuery(id+"F31.wireOp",EDGE,"E96.left")])]});
            var Q9;
            Q9=makeQuery(id+"F32.opExtrude","SWEPT_EDGE",EDGE,{"disambiguationData":[OSD([sQuery(id+"F31.wireOp",EDGE,"E89"),sQuery(id+"F31.wireOp",EDGE,"E90")])]});
            var Q10;
            Q10=makeQuery(id+"F32.opExtrude","SWEPT_EDGE",EDGE,{"disambiguationData":[OSD([sQuery(id+"F31.wireOp",EDGE,"E96.top"),sQuery(id+"F31.wireOp",EDGE,"E96.right")])]});
            var Q11;
            Q11=makeQuery(id+"F32.opExtrude","SWEPT_EDGE",EDGE,{"disambiguationData":[OSD([sQuery(id+"F31.wireOp",EDGE,"E93"),sQuery(id+"F31.wireOp",EDGE,"E94")])]});
            var Q12;
            Q12=makeQuery(id+"F32.opExtrude","SWEPT_EDGE",EDGE,{"disambiguationData":[OSD([sQuery(id+"F31.wireOp",EDGE,"E92"),sQuery(id+"F31.wireOp",EDGE,"E93")])]});
            var Q13;
            Q13=makeQuery(id+"F32.opExtrude","SWEPT_EDGE",EDGE,{"disambiguationData":[OSD([sQuery(id+"F31.wireOp",EDGE,"E96.bottom"),sQuery(id+"F31.wireOp",EDGE,"E96.right")])]});
            fillet(context, id + "F41", {"entities" : qUnion([Q0, Q1, Q2, Q3, Q4, Q5, Q6, Q7, Q8, Q9, Q10, Q11, Q12, Q13]), "radius" : 1 * mm, "tangentPropagation" : true, "allowEdgeOverflow" : false});
        }
        {
            var Q0;
            Q0=makeQuery(id+"F32.opExtrude","SWEPT_BODY",BODY,{"disambiguationData":[OSD([sQuery(id+"F31.wireOp",EDGE,"HWwBU39I-d0Rr-kACm-DON5-1Ibhyw6kzuj5"),sQuery(id+"F31.wireOp",EDGE,"E60"),sQuery(id+"F31.wireOp",EDGE,"E61"),sQuery(id+"F31.wireOp",EDGE,"E62"),sQuery(id+"F31.wireOp",EDGE,"E63"),sQuery(id+"F31.wireOp",EDGE,"E64"),sQuery(id+"F31.wireOp",EDGE,"E65"),sQuery(id+"F31.wireOp",EDGE,"E66"),sQuery(id+"F31.wireOp",EDGE,"E74"),sQuery(id+"F31.wireOp",EDGE,"E75"),sQuery(id+"F31.wireOp",EDGE,"E76"),sQuery(id+"F31.wireOp",EDGE,"E77"),sQuery(id+"F31.wireOp",EDGE,"E78"),sQuery(id+"F31.wireOp",EDGE,"E79"),sQuery(id+"F31.wireOp",EDGE,"E80"),sQuery(id+"F31.wireOp",EDGE,"E81"),sQuery(id+"F31.wireOp",EDGE,"bY2D1s1w-CCC7-tj32-Su82-opb9EQVePSfk"),sQuery(id+"F31.wireOp",EDGE,"8NsvQF51-Jp1q-trSI-gVP7-qAqv6czTjHgz"),sQuery(id+"F31.wireOp",EDGE,"k6c7TyGP-aetQ-e4CA-Xoma-WksUmgi34R7H"),sQuery(id+"F31.wireOp",EDGE,"E85"),sQuery(id+"F31.wireOp",EDGE,"E86"),sQuery(id+"F31.wireOp",EDGE,"E87.trimOffspring")])]});
            var Q1;
            Q1=qCreatedBy(makeId("Front.planeOp"),FACE);
            mirror(context, id + "F42", {"operationType" : NewBodyOperationType.ADD, "entities" : qUnion([Q0]), "mirrorPlane" : qUnion([Q1])});
        }
        {
            var Q0;
            Q0=qCreatedBy(makeId("Top.planeOp"),FACE);
            var sketch = newSketch(context, id + "F43", { "sketchPlane" : qUnion([Q0])});
            skLineSegment(sketch, "E147", {"start": v(310, 22.8) * mm, "end": v(310, -18) * mm});
            skLineSegment(sketch, "E148", {"start": v(310, -18) * mm, "end": v(370.1, -18) * mm});
            skLineSegment(sketch, "E149", {"start": v(370.1, -9) * mm, "end": v(369.1, -9) * mm});
            skLineSegment(sketch, "E150", {"start": v(369.1, -9) * mm, "end": v(369.1, 22.8) * mm});
            skLineSegment(sketch, "E151", {"start": v(369.1, 22.8) * mm, "end": v(310, 22.8) * mm});
            skLineSegment(sketch, "E152.bottom", {"start": v(313, 19.8) * mm, "end": v(332.1, 19.8) * mm});
            skLineSegment(sketch, "E152.top", {"start": v(313, -15) * mm, "end": v(332.1, -15) * mm});
            skLineSegment(sketch, "E152.left", {"start": v(313, 19.8) * mm, "end": v(313, -15) * mm});
            skLineSegment(sketch, "E152.right", {"start": v(332.1, 19.8) * mm, "end": v(332.1, -15) * mm});
            skLineSegment(sketch, "E153.bottom", {"start": v(337.1, 19.8) * mm, "end": v(366.1, 19.8) * mm});
            skLineSegment(sketch, "E153.top", {"start": v(337.1, -15) * mm, "end": v(366.1, -15) * mm});
            skLineSegment(sketch, "E153.left", {"start": v(337.1, 19.8) * mm, "end": v(337.1, -15) * mm});
            skLineSegment(sketch, "E153.right", {"start": v(366.1, 19.8) * mm, "end": v(366.1, -15) * mm});
            skLineSegment(sketch, "E154", {"start": v(370.1, -18) * mm, "end": v(370.1, -9) * mm});
            skSolve(sketch);
        }
        {
            var Q0;
            Q0 = qSketchRegion(id + "F43", true);
            extrude(context, id + "F44", {"entities" : qUnion([Q0]), "depth" : 3 * mm});
        }
        {
            var Q0;
            Q0=makeQuery(id+"F44.opExtrude","SWEPT_EDGE",EDGE,{"disambiguationData":[OSD([sQuery(id+"F43.wireOp",EDGE,"E147"),sQuery(id+"F43.wireOp",EDGE,"E148")])]});
            var Q1;
            Q1=makeQuery(id+"F44.opExtrude","SWEPT_EDGE",EDGE,{"disambiguationData":[OSD([sQuery(id+"F43.wireOp",EDGE,"E148"),sQuery(id+"F43.wireOp",EDGE,"E154")])]});
            var Q2;
            Q2=makeQuery(id+"F44.opExtrude","SWEPT_EDGE",EDGE,{"disambiguationData":[OSD([sQuery(id+"F43.wireOp",EDGE,"E150"),sQuery(id+"F43.wireOp",EDGE,"E151")])]});
            var Q3;
            Q3=makeQuery(id+"F44.opExtrude","SWEPT_EDGE",EDGE,{"disambiguationData":[OSD([sQuery(id+"F43.wireOp",EDGE,"E147"),sQuery(id+"F43.wireOp",EDGE,"E151")])]});
            fillet(context, id + "F45", {"entities" : qUnion([Q0, Q1, Q2, Q3]), "radius" : 1 * mm, "tangentPropagation" : true, "allowEdgeOverflow" : false});
        }
        {
            var Q0;
            Q0=makeQuery(id+"F44.opExtrude","CAP_FACE",FACE,{"disambiguationData":[OSD([sQuery(id+"F43.wireOp",EDGE,"E147"),sQuery(id+"F43.wireOp",EDGE,"E148"),sQuery(id+"F43.wireOp",EDGE,"E149"),sQuery(id+"F43.wireOp",EDGE,"E150"),sQuery(id+"F43.wireOp",EDGE,"E151"),sQuery(id+"F43.wireOp",EDGE,"E152.bottom"),sQuery(id+"F43.wireOp",EDGE,"E152.top"),sQuery(id+"F43.wireOp",EDGE,"E152.left"),sQuery(id+"F43.wireOp",EDGE,"E152.right"),sQuery(id+"F43.wireOp",EDGE,"E153.bottom"),sQuery(id+"F43.wireOp",EDGE,"E153.top"),sQuery(id+"F43.wireOp",EDGE,"E153.left"),sQuery(id+"F43.wireOp",EDGE,"E153.right"),sQuery(id+"F43.wireOp",EDGE,"E154")])],"isStart":false});
            var sketch = newSketch(context, id + "F46", { "sketchPlane" : qUnion([Q0])});
            skLineSegment(sketch, "E155.bottom", {"start": v(306.2, 26.55) * mm, "end": v(372.9, 26.55) * mm});
            skLineSegment(sketch, "E155.top", {"start": v(306.2, -21.65) * mm, "end": v(372.9, -21.65) * mm});
            skLineSegment(sketch, "E155.left", {"start": v(306.2, 26.55) * mm, "end": v(306.2, -21.65) * mm});
            skLineSegment(sketch, "E155.right", {"start": v(372.9, 26.55) * mm, "end": v(372.9, -21.65) * mm});
            skLineSegment(sketch, "E156.top", {"start": v(309.2, -18.65) * mm, "end": v(369.9, -18.65) * mm});
            skLineSegment(sketch, "E156.right", {"start": v(369.9, 23.55) * mm, "end": v(369.9, -18.65) * mm});
            skLineSegment(sketch, "E157", {"start": v(309.2, -18.65) * mm, "end": v(309.2, 23.55) * mm});
            skLineSegment(sketch, "E158", {"start": v(309.2, 23.55) * mm, "end": v(369.9, 23.55) * mm});
            skSolve(sketch);
        }
        {
            var Q0;
            Q0 = qSketchRegion(id + "F46", true);
            extrude(context, id + "F47", {"entities" : qUnion([Q0]), "operationType" : NewBodyOperationType.ADD, "depth" : 5 * mm});
        }
        {
            var Q0;
            Q0=makeQuery(id+"F47.opExtrude","SWEPT_FACE",FACE,{"disambiguationData":[OSD([sQuery(id+"F46.wireOp",EDGE,"E155.right")])]});
            var sketch = newSketch(context, id + "F48", { "sketchPlane" : qUnion([Q0])});
            skLineSegment(sketch, "E159.bottom", {"start": v(-21.65, 3) * mm, "end": v(26.55, 3) * mm});
            skLineSegment(sketch, "E159.top", {"start": v(-21.65, 4.5) * mm, "end": v(26.55, 4.5) * mm});
            skLineSegment(sketch, "E159.left", {"start": v(-21.65, 3) * mm, "end": v(-21.65, 4.5) * mm});
            skLineSegment(sketch, "E159.right", {"start": v(26.55, 3) * mm, "end": v(26.55, 4.5) * mm});
            skSolve(sketch);
        }
        {
            var Q0;
            Q0 = qSketchRegion(id + "F48", true);
            var Q1;
            Q1=makeQuery(id+"F47.opExtrude","SWEPT_FACE",FACE,{"disambiguationData":[OSD([sQuery(id+"F46.wireOp",EDGE,"E155.left")])]});
            extrude(context, id + "F49", {"entities" : qUnion([Q0]), "operationType" : NewBodyOperationType.ADD, "endBound" : BoundingType.UP_TO_SURFACE, "oppositeDirection" : true, "endBoundEntityFace" : qUnion([Q1]), "depth" : 25 * mm});
        }
        {
            var Q0;
            Q0=makeQuery(id+"F49.boolean.opBoolean","SPLIT",FACE,{"disambiguationData":[TD([makeQuery(id+"F44.opExtrude","SWEPT_FACE",FACE,{"disambiguationData":[OSD([sQuery(id+"F43.wireOp",EDGE,"E153.bottom")])]})])],"derivedFrom":makeQuery(id+"F49.opExtrude","SWEPT_FACE",FACE,{"disambiguationData":[OSD([sQuery(id+"F48.wireOp",EDGE,"E159.bottom")])]})});
            var sketch = newSketch(context, id + "F50", { "sketchPlane" : qUnion([Q0])});
            skLineSegment(sketch, "E160.bottom", {"start": v(313, 15) * mm, "end": v(332.1, 15) * mm});
            skLineSegment(sketch, "E160.top", {"start": v(313, -19.8) * mm, "end": v(332.1, -19.8) * mm});
            skLineSegment(sketch, "E160.left", {"start": v(313, 15) * mm, "end": v(313, -19.8) * mm});
            skLineSegment(sketch, "E160.right", {"start": v(332.1, 15) * mm, "end": v(332.1, -19.8) * mm});
            skLineSegment(sketch, "E161.bottom", {"start": v(337.1, 15) * mm, "end": v(366.1, 15) * mm});
            skLineSegment(sketch, "E161.top", {"start": v(337.1, -19.8) * mm, "end": v(366.1, -19.8) * mm});
            skLineSegment(sketch, "E161.left", {"start": v(337.1, 15) * mm, "end": v(337.1, -19.8) * mm});
            skLineSegment(sketch, "E162", {"start": v(366.1, 15) * mm, "end": v(366.1, 10.1) * mm});
            skLineSegment(sketch, "E163", {"start": v(366.1, 10.1) * mm, "end": v(367.1, 10.1) * mm});
            skLineSegment(sketch, "E164", {"start": v(367.1, 10.1) * mm, "end": v(367.1, -14.9) * mm});
            skLineSegment(sketch, "E165", {"start": v(367.1, -14.9) * mm, "end": v(366.1, -14.9) * mm});
            skLineSegment(sketch, "E166", {"start": v(366.1, -14.9) * mm, "end": v(366.1, -19.8) * mm});
            skSolve(sketch);
        }
        {
            var Q0;
            Q0 = qSketchRegion(id + "F50", true);
            extrude(context, id + "F51", {"entities" : qUnion([Q0]), "operationType" : NewBodyOperationType.REMOVE, "endBound" : BoundingType.THROUGH_ALL, "oppositeDirection" : true, "depth" : 25 * mm, "hasSecondDirection" : true, "secondDirectionBound" : SecondDirectionBoundingType.THROUGH_ALL, "secondDirectionOppositeDirection" : false, "secondDirectionDepth" : 25 * mm});
        }
        {
            var Q0;
            Q0=qCreatedBy(makeId("Top.planeOp"),FACE);
            var sketch = newSketch(context, id + "F52", { "sketchPlane" : qUnion([Q0])});
            skLineSegment(sketch, "E167.bottom", {"start": v(-210, 12) * mm, "end": v(-170, 12) * mm});
            skLineSegment(sketch, "E167.top", {"start": v(-210, -12) * mm, "end": v(-170, -12) * mm});
            skLineSegment(sketch, "E167.left", {"start": v(-210, 12) * mm, "end": v(-210, -12) * mm});
            skLineSegment(sketch, "E167.right", {"start": v(-170, 12) * mm, "end": v(-170, -12) * mm});
            skPoint(sketch, "E168", {"position": v(-170, 0) * mm});
            skLineSegment(sketch, "E169", {"start": v(-170, 0) * mm, "end": v(-210, 0) * mm, "construction": true});
            skCircle(sketch, "E170", {"center": v(-204, 0) * mm, "radius": 2 * mm});
            skCircle(sketch, "E171", {"center": v(-178, 0) * mm, "radius": 2 * mm});
            skCircle(sketch, "E172", {"center": v(-191, 0) * mm, "radius": 4 * mm});
            skSolve(sketch);
        }
        {
            var Q0;
            Q0 = qSketchRegion(id + "F52", true);
            extrude(context, id + "F53", {"entities" : qUnion([Q0]), "depth" : 5 * mm});
        }
        {
            var Q0;
            Q0=makeQuery(id+"F53.opExtrude","CAP_FACE",FACE,{"disambiguationData":[OSD([sQuery(id+"F52.wireOp",EDGE,"E167.bottom"),sQuery(id+"F52.wireOp",EDGE,"E167.top"),sQuery(id+"F52.wireOp",EDGE,"E167.left"),sQuery(id+"F52.wireOp",EDGE,"E167.right"),sQuery(id+"F52.wireOp",EDGE,"E170"),sQuery(id+"F52.wireOp",EDGE,"E171")])],"isStart":false});
            var sketch = newSketch(context, id + "F54", { "sketchPlane" : qUnion([Q0])});
            skLineSegment(sketch, "E173", {"start": v(-207, 12) * mm, "end": v(-210, 12) * mm});
            skLineSegment(sketch, "E174", {"start": v(-210, 12) * mm, "end": v(-210, -12) * mm});
            skLineSegment(sketch, "E175", {"start": v(-210, -12) * mm, "end": v(-170, -12) * mm});
            skLineSegment(sketch, "E176", {"start": v(-170, -12) * mm, "end": v(-170, -8) * mm});
            skLineSegment(sketch, "E177", {"start": v(-170, -8) * mm, "end": v(-207, -8) * mm});
            skLineSegment(sketch, "E178", {"start": v(-207, -8) * mm, "end": v(-207, 12) * mm});
            skSolve(sketch);
        }
        {
            var Q0;
            Q0=qCreatedBy(makeId("Top.planeOp"),FACE);
            cPlane(context, id + "F55", {"entities" : qUnion([Q0]), "cplaneType" : CPlaneType.OFFSET, "offset" : 150 * mm, "width" : 150 * mm, "height" : 150 * mm});
        }
        {
            var Q0;
            Q0=qCreatedBy(id+"F55.planeOp",FACE);
            var sketch = newSketch(context, id + "F56", { "sketchPlane" : qUnion([Q0])});
            skLineSegment(sketch, "E179.left", {"start": v(-202, -4) * mm, "end": v(-202, -12) * mm});
            skLineSegment(sketch, "E179.right", {"start": v(-199, -4) * mm, "end": v(-199, -8) * mm});
            skLineSegment(sketch, "E180", {"start": v(-199, -8) * mm, "end": v(-196, -8) * mm});
            skLineSegment(sketch, "E181", {"start": v(-196, -8) * mm, "end": v(-196, -12) * mm});
            skLineSegment(sketch, "E182", {"start": v(-196, -12) * mm, "end": v(-202, -12) * mm});
            skLineSegment(sketch, "E183", {"start": v(-202, -4) * mm, "end": v(-199, -4) * mm});
            skSolve(sketch);
        }
        {
            var Q1;
            Q1=makeQuery(id+"F54.imprint","IMPRINT",FACE,{"disambiguationData":[TD([[makeQuery(id+"F54.imprint","IMPRINT",EDGE,{"derivedFrom":sQuery(id+"F54.wireOp",EDGE,"E173")}),-1.0]])]});
            var Q2;
            Q2=makeQuery(id+"F56.imprint","IMPRINT",FACE,{"disambiguationData":[TD([[makeQuery(id+"F56.imprint","IMPRINT",EDGE,{"derivedFrom":sQuery(id+"F56.wireOp",EDGE,"E179.left")}),1.0]])]});
            loft(context, id + "F57", {"operationType" : NewBodyOperationType.ADD, "sheetProfilesArray" : [{ "sheetProfileEntities" : qUnion([Q1]) }, { "sheetProfileEntities" : qUnion([Q2]) }]});
        }
        {
            var Q0;
            Q0=qCreatedBy(makeId("Front.planeOp"),FACE);
            var sketch = newSketch(context, id + "F58", { "sketchPlane" : qUnion([Q0])});
            skLineSegment(sketch, "E184", {"start": v(-176.51, 13) * mm, "end": v(-205.44, 33.25) * mm});
            skLineSegment(sketch, "E185", {"start": v(-205.44, 33.25) * mm, "end": v(-205.17, 38) * mm});
            skLineSegment(sketch, "E186", {"start": v(-205.17, 38) * mm, "end": v(-185.25, 61.74) * mm});
            skLineSegment(sketch, "E187", {"start": v(-185.25, 61.74) * mm, "end": v(-176.51, 13) * mm});
            skLineSegment(sketch, "E188", {"start": v(-186.17, 66.87) * mm, "end": v(-204.8, 44.66) * mm});
            skLineSegment(sketch, "E189", {"start": v(-204.8, 44.66) * mm, "end": v(-202.45, 87.36) * mm});
            skLineSegment(sketch, "E190", {"start": v(-202.45, 87.36) * mm, "end": v(-187.1, 72) * mm});
            skLineSegment(sketch, "E191", {"start": v(-187.1, 72) * mm, "end": v(-186.17, 66.87) * mm});
            skLineSegment(sketch, "E192", {"start": v(-188.33, 78.9) * mm, "end": v(-199.49, 141.11) * mm});
            skLineSegment(sketch, "E193", {"start": v(-199.49, 141.11) * mm, "end": v(-202.16, 92.72) * mm});
            skLineSegment(sketch, "E194", {"start": v(-202.16, 92.72) * mm, "end": v(-188.33, 78.9) * mm});
            skLineSegment(sketch, "E195", {"start": v(-175.51, 7.42) * mm, "end": v(-205.7, 28.55) * mm, "construction": true});
            skLineSegment(sketch, "E196", {"start": v(-205.7, 28.55) * mm, "end": v(-207, 5) * mm, "construction": true});
            skLineSegment(sketch, "E197", {"start": v(-207, 5) * mm, "end": v(-175.08, 5) * mm, "construction": true});
            skLineSegment(sketch, "E198", {"start": v(-175.08, 5) * mm, "end": v(-175.51, 7.42) * mm, "construction": true});
            skSolve(sketch);
        }
        {
            var Q0;
            Q0 = qSketchRegion(id + "F58", true);
            extrude(context, id + "F59", {"entities" : qUnion([Q0]), "operationType" : NewBodyOperationType.REMOVE, "endBound" : BoundingType.THROUGH_ALL, "oppositeDirection" : true, "depth" : 25 * mm, "hasSecondDirection" : true, "secondDirectionBound" : SecondDirectionBoundingType.THROUGH_ALL, "secondDirectionOppositeDirection" : false, "secondDirectionDepth" : 25 * mm});
        }
        {
            var Q0;
            Q0=makeQuery(id+"F53.opExtrude","CAP_FACE",FACE,{"disambiguationData":[OSD([sQuery(id+"F52.wireOp",EDGE,"E167.bottom"),sQuery(id+"F52.wireOp",EDGE,"E167.top"),sQuery(id+"F52.wireOp",EDGE,"E167.left"),sQuery(id+"F52.wireOp",EDGE,"E167.right"),sQuery(id+"F52.wireOp",EDGE,"E170"),sQuery(id+"F52.wireOp",EDGE,"E171"),sQuery(id+"F52.wireOp",EDGE,"E172")])],"isStart":false});
            var sketch = newSketch(context, id + "F60", { "sketchPlane" : qUnion([Q0])});
            skLineSegment(sketch, "E199.bottom", {"start": v(-175, 12) * mm, "end": v(-170, 12) * mm});
            skLineSegment(sketch, "E199.top", {"start": v(-175, -8) * mm, "end": v(-170, -8) * mm});
            skLineSegment(sketch, "E199.left", {"start": v(-175, 12) * mm, "end": v(-175, -8) * mm});
            skLineSegment(sketch, "E199.right", {"start": v(-170, 12) * mm, "end": v(-170, -8) * mm});
            skSolve(sketch);
        }
        {
            var Q0;
            {var subQ0=sQuery(id+"F60.wireOp",EDGE,"E199.left");Q0=makeQuery(id+"F60.imprint","IMPRINT",FACE,{"disambiguationData":[TD([[makeQuery(id+"F60.imprint","IMPRINT",EDGE,{"derivedFrom":subQ0}),-1.0]])]});}
            cPlane(context, id + "F61", {"entities" : qUnion([Q0]), "cplaneType" : CPlaneType.OFFSET, "offset" : 8 * mm, "width" : 150 * mm, "height" : 150 * mm});
        }
        {
            var Q0;
            Q0=qCreatedBy(id+"F61.planeOp",FACE);
            var sketch = newSketch(context, id + "F62", { "sketchPlane" : qUnion([Q0])});
            skLineSegment(sketch, "E200.bottom", {"start": v(-176.51, -7.9) * mm, "end": v(-171.43, -7.9) * mm});
            skLineSegment(sketch, "E200.top", {"start": v(-176.51, -8) * mm, "end": v(-171.43, -8) * mm});
            skLineSegment(sketch, "E200.left", {"start": v(-176.51, -7.9) * mm, "end": v(-176.51, -8) * mm});
            skLineSegment(sketch, "E200.right", {"start": v(-171.43, -7.9) * mm, "end": v(-171.43, -8) * mm});
            skSolve(sketch);
        }
        {
            var Q1;
            Q1 = qSketchRegion(id + "F60", true);
            var Q2;
            Q2 = qSketchRegion(id + "F62", true);
            loft(context, id + "F63", {"operationType" : NewBodyOperationType.ADD, "sheetProfilesArray" : [{ "sheetProfileEntities" : qUnion([Q1]) }, { "sheetProfileEntities" : qUnion([Q2]) }]});
        }
        {
            var Q0;
            Q0=makeQuery(id+"F53.opExtrude","CAP_FACE",FACE,{"disambiguationData":[OSD([sQuery(id+"F52.wireOp",EDGE,"E167.bottom"),sQuery(id+"F52.wireOp",EDGE,"E167.top"),sQuery(id+"F52.wireOp",EDGE,"E167.left"),sQuery(id+"F52.wireOp",EDGE,"E167.right"),sQuery(id+"F52.wireOp",EDGE,"E170"),sQuery(id+"F52.wireOp",EDGE,"E171"),sQuery(id+"F52.wireOp",EDGE,"E172")])],"isStart":false});
            var sketch = newSketch(context, id + "F64", { "sketchPlane" : qUnion([Q0])});
            skLineSegment(sketch, "E201.bottom", {"start": v(-210, 12) * mm, "end": v(-170, 12) * mm});
            skLineSegment(sketch, "E201.left", {"start": v(-210, 12) * mm, "end": v(-210, 9) * mm});
            skLineSegment(sketch, "E201.right", {"start": v(-170, 12) * mm, "end": v(-170, 9) * mm});
            skLineSegment(sketch, "E202", {"start": v(-210, 9) * mm, "end": v(-170, 9) * mm});
            skSolve(sketch);
        }
        {
            var Q0;
            Q0 = qSketchRegion(id + "F64", true);
            extrude(context, id + "F65", {"entities" : qUnion([Q0]), "operationType" : NewBodyOperationType.ADD, "depth" : 1 * mm});
        }
        {
            var Q0;
            Q0=qCreatedBy(makeId("Front.planeOp"),FACE);
            var sketch = newSketch(context, id + "F66", { "sketchPlane" : qUnion([Q0])});
            skLineSegment(sketch, "E203.bottom", {"start": v(-198.5, 7) * mm, "end": v(-183.5, 7) * mm});
            skLineSegment(sketch, "E203.top", {"start": v(-198.5, 5) * mm, "end": v(-183.5, 5) * mm});
            skLineSegment(sketch, "E203.left", {"start": v(-198.5, 7) * mm, "end": v(-198.5, 5) * mm});
            skLineSegment(sketch, "E203.right", {"start": v(-183.5, 7) * mm, "end": v(-183.5, 5) * mm});
            skLineSegment(sketch, "E204.bottom", {"start": v(-206.89, 7) * mm, "end": v(-202.89, 7) * mm});
            skLineSegment(sketch, "E204.top", {"start": v(-206.89, 5) * mm, "end": v(-202.89, 5) * mm});
            skLineSegment(sketch, "E204.left", {"start": v(-206.89, 7) * mm, "end": v(-206.89, 5) * mm});
            skLineSegment(sketch, "E204.right", {"start": v(-202.89, 7) * mm, "end": v(-202.89, 5) * mm});
            skLineSegment(sketch, "E205.bottom", {"start": v(-179.38, 7) * mm, "end": v(-175.38, 7) * mm});
            skLineSegment(sketch, "E205.top", {"start": v(-179.38, 5) * mm, "end": v(-175.38, 5) * mm});
            skLineSegment(sketch, "E205.left", {"start": v(-179.38, 7) * mm, "end": v(-179.38, 5) * mm});
            skLineSegment(sketch, "E205.right", {"start": v(-175.38, 7) * mm, "end": v(-175.38, 5) * mm});
            skSolve(sketch);
        }
        {
            var Q0;
            Q0 = qSketchRegion(id + "F66", true);
            extrude(context, id + "F67", {"entities" : qUnion([Q0]), "operationType" : NewBodyOperationType.REMOVE, "endBound" : BoundingType.THROUGH_ALL, "oppositeDirection" : true, "depth" : 25 * mm, "hasSecondDirection" : true, "secondDirectionBound" : SecondDirectionBoundingType.THROUGH_ALL, "secondDirectionOppositeDirection" : false, "secondDirectionDepth" : 25 * mm});
        }
        {
            var Q0;
            Q0=qCreatedBy(makeId("Top.planeOp"),FACE);
            var sketch = newSketch(context, id + "F68", { "sketchPlane" : qUnion([Q0])});
            skArc(sketch, "E206", {"start": v(-275, 4) * mm, "mid": v(-277.5, 6.5) * mm, "end": v(-280, 4) * mm});
            skLineSegment(sketch, "E207", {"start": v(-280, 4) * mm, "end": v(-280, 0) * mm});
            skLineSegment(sketch, "E208", {"start": v(-280, 0) * mm, "end": v(-285, 0) * mm});
            skLineSegment(sketch, "E209", {"start": v(-285, 0) * mm, "end": v(-285, 86.75) * mm});
            skLineSegment(sketch, "E210", {"start": v(-285, 86.75) * mm, "end": v(-231.48, 100.1) * mm});
            skLineSegment(sketch, "E211", {"start": v(-230.99, 96.1) * mm, "end": v(-279.5, 84) * mm});
            skLineSegment(sketch, "E212", {"start": v(-279.5, 84) * mm, "end": v(-279.5, 81) * mm});
            skLineSegment(sketch, "E213", {"start": v(-275, 4) * mm, "end": v(-275, 0) * mm});
            skLineSegment(sketch, "E214", {"start": v(-275, 0) * mm, "end": v(-270, 0) * mm});
            skLineSegment(sketch, "E215", {"start": v(-270, 0) * mm, "end": v(-270, 8) * mm});
            skLineSegment(sketch, "E216", {"start": v(-270, 8) * mm, "end": v(-279.5, 20) * mm});
            skLineSegment(sketch, "E217", {"start": v(-279.5, 20) * mm, "end": v(-279.5, 32) * mm});
            skArc(sketch, "E218", {"start": v(-279.5, 81) * mm, "mid": v(-281.51, 56.5) * mm, "end": v(-279.5, 32) * mm});
            skLineSegment(sketch, "E219", {"start": v(-230.99, 96.1) * mm, "end": v(-205.99, 96.1) * mm});
            skLineSegment(sketch, "E220", {"start": v(-205.99, 96.1) * mm, "end": v(-205.99, 100.1) * mm});
            skLineSegment(sketch, "E221", {"start": v(-205.99, 100.1) * mm, "end": v(-231.48, 100.1) * mm});
            skSolve(sketch);
        }
        {
            var Q0;
            Q0 = qSketchRegion(id + "F68", true);
            extrude(context, id + "F69", {"entities" : qUnion([Q0]), "depth" : 50 * mm});
        }
        {
            var Q0;
            Q0=makeQuery(id+"F69.opExtrude","SWEPT_FACE",FACE,{"disambiguationData":[OSD([sQuery(id+"F68.wireOp",EDGE,"E209")])]});
            var sketch = newSketch(context, id + "F70", { "sketchPlane" : qUnion([Q0])});
            skCircle(sketch, "E222", {"center": v(-59, 25) * mm, "radius": 11.5 * mm});
            skLineSegment(sketch, "E223", {"start": v(-59, 0) * mm, "end": v(-59, 50) * mm, "construction": true});
            skSolve(sketch);
        }
        {
            var Q0;
            Q0=makeQuery(id+"F70.imprint","IMPRINT",FACE,{"disambiguationData":[TD([[makeQuery(id+"F70.imprint","IMPRINT",EDGE,{"derivedFrom":sQuery(id+"F70.wireOp",EDGE,"E222")}),1.0]])]});
            var Q1;
            Q1=sQuery(id+"F70.wireOp",EDGE,"E222");
            extrude(context, id + "F71", {"entities" : qUnion([Q0]), "operationType" : NewBodyOperationType.REMOVE, "surfaceEntities" : qUnion([Q1]), "endBound" : BoundingType.UP_TO_NEXT, "oppositeDirection" : true, "depth" : 25 * mm});
        }
        {
            var Q0;
            Q0=makeQuery(id+"F69.opExtrude","SWEPT_FACE",FACE,{"disambiguationData":[OSD([sQuery(id+"F68.wireOp",EDGE,"E221")])]});
            var sketch = newSketch(context, id + "F72", { "sketchPlane" : qUnion([Q0])});
            skLineSegment(sketch, "E224.bottom", {"start": v(221.99, 19) * mm, "end": v(216.99, 19) * mm});
            skLineSegment(sketch, "E224.top", {"start": v(221.99, 31) * mm, "end": v(216.99, 31) * mm});
            skLineSegment(sketch, "E224.left", {"start": v(221.99, 19) * mm, "end": v(221.99, 31) * mm});
            skLineSegment(sketch, "E224.right", {"start": v(216.99, 19) * mm, "end": v(216.99, 31) * mm});
            skPoint(sketch, "E225", {"position": v(205.99, 25) * mm});
            skLineSegment(sketch, "E226", {"start": v(216.99, 25) * mm, "end": v(205.99, 25) * mm, "construction": true});
            skSolve(sketch);
        }
        {
            var Q0;
            Q0 = qSketchRegion(id + "F72", true);
            extrude(context, id + "F73", {"entities" : qUnion([Q0]), "operationType" : NewBodyOperationType.REMOVE, "endBound" : BoundingType.UP_TO_NEXT, "oppositeDirection" : true, "depth" : 25 * mm});
        }
    });
